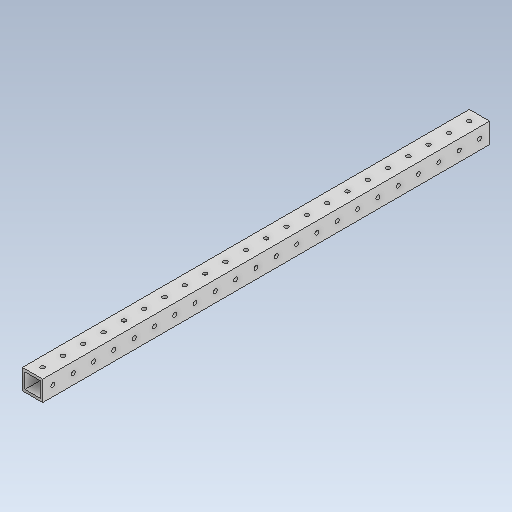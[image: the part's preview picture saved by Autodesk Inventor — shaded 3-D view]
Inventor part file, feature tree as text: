
AUTODESK INVENTOR PART (.ipt)
format: ipt  version: 2020 (Build 240168000, 168)  size: 211,968 bytes
history: native  units: in
note: dims shown in document units (in); Inventor stores cm internally (conversion verified against a paired STEP export)
features: other x3, sketch x3
ambient origin geometry x8: Origin, YZ Plane, XZ Plane, XY Plane, X Axis, Y Axis, Z Axis, Center Point
bodies: Solid1 (feature_tree)
feature tree (6):
  other  "1x1x18.ipt"
  other  "Solid1::1x1x18.ipt"
  other  "TaggingFeature1"
  sketch  "Sketch1"  dims[d0=0.3937in]
  sketch  "Sketch2"
  sketch  "Sketch3"
